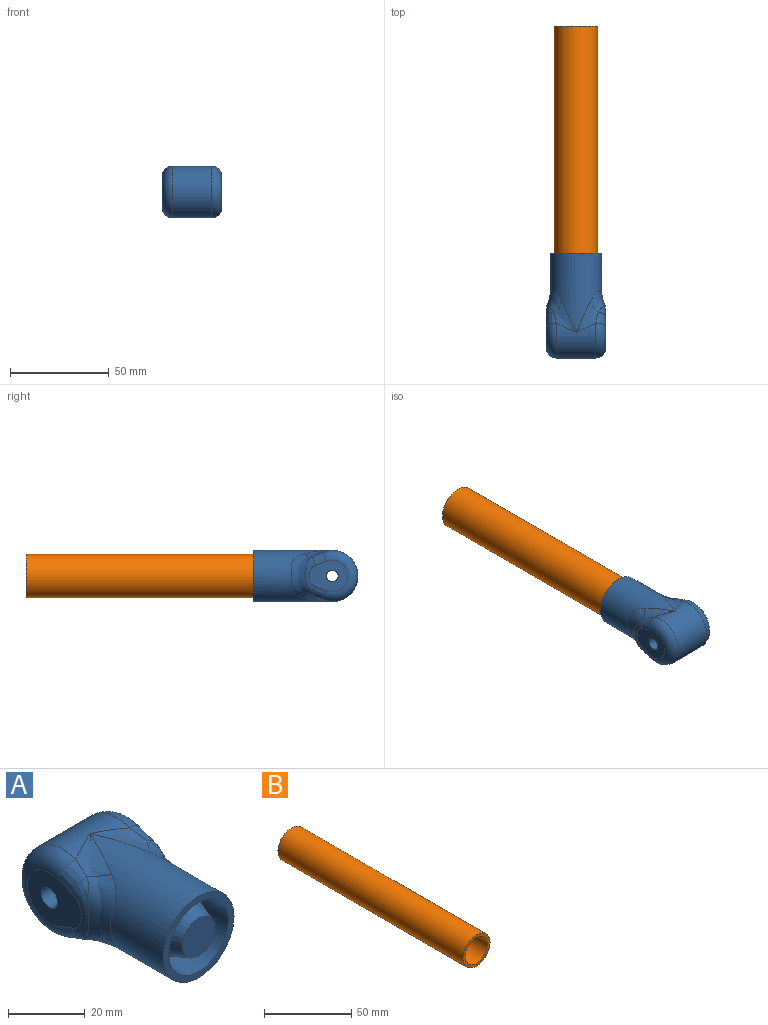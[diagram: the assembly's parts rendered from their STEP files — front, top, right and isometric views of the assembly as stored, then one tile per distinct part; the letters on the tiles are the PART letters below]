
ASSEMBLY  parts=2 mates=1
PART A: 26 faces, bbox 32.6x54.1x30.8 mm
  f0: cylinder r=11mm len=35mm, axis (0,1,0), area 2419mm2, adj f1,f5
  f1: plane 22x22mm, normal (0,-1,0), area 125.7mm2, adj f0,f2
  f2: cylinder r=9mm len=26.76mm, axis (0,1,0), area 1513.1mm2, adj f1,f3
  f3: cone r=6mm half-angle=20deg, axis (0,1,0), area 413.3mm2, adj f2,f4
  f4: plane 12x12mm, normal (0,-1,0), area 113.1mm2, adj f3
  f5: plane 26x26mm, normal (0,-1,0), area 150.8mm2, adj f0,f6
  f6: cylinder r=13mm len=40mm, axis (0,1,0), area 2262.5mm2, adj f5,f7,f20,f21,f22,f23,f24,f25
  f7: bspline ~16.32x16.32mm, area 62.4mm2, adj f6,f8,f19,f20
  f8: bspline ~12.76x9.34mm, area 42.6mm2, adj f7,f9,f17,f18
  f9: plane 19.77x16mm, normal (1,0,0), area 216.3mm2, adj f8,f10,f16,f17,f18
  f10: cylinder r=3mm len=30mm, axis (-1,0,0), area 565.5mm2, adj f9,f11
  f11: plane 19.77x16mm, normal (-1,0,0), area 216.3mm2, adj f10,f12,f13,f14,f15
  f12: bspline ~15.49x11.01mm, area 42.6mm2, adj f11,f13,f15,f24
  f13: bspline ~20.29x5.91mm, area 66.1mm2, adj f11,f12,f14,f23
  f14: bspline ~15.07x10.85mm, area 42.6mm2, adj f11,f13,f15,f22
  f15: torus R=8mm, axis (1,0,0), area 340.1mm2, adj f11,f12,f14,f19
  f16: bspline ~9.9x7.76mm, area 42.6mm2, adj f9,f17,f18,f21
  f17: bspline ~20.81x6.73mm, area 66.1mm2, adj f8,f9,f16,f20
  f18: torus R=8mm, axis (1,0,0), area 340.1mm2, adj f8,f9,f16,f19
  f19: cylinder r=13mm len=26mm, axis (-1,0,0), area 911.8mm2, adj f7,f15,f18,f21,f22,f24,f25
  f20: bspline ~22.75x14.97mm, area 152.8mm2, adj f6,f7,f17,f21
  f21: bspline ~16.32x16.32mm, area 47.2mm2, adj f6,f16,f19,f20
  f22: bspline ~16.32x16.32mm, area 47.2mm2, adj f6,f14,f19,f23
  f23: bspline ~22.75x14.97mm, area 152.8mm2, adj f6,f13,f22,f24
  f24: bspline ~16.32x16.32mm, area 54.8mm2, adj f6,f12,f19,f23
  f25: bspline ~3.66x3.66mm, area 0mm2, adj f6,f19
PART B: 4 faces, bbox 22x150x22 mm
  f0: cylinder r=9mm len=150mm, axis (0,1,0), area 8482.3mm2, adj f2,f3
  f1: cylinder r=11mm len=150mm, axis (0,1,0), area 10367.3mm2, adj f2,f3
  f2: plane 22x22mm, normal (0,-1,0), area 125.7mm2, adj f0,f1
  f3: plane 22x22mm, normal (0,1,0), area 125.7mm2, adj f0,f1
PLACE A rot(axis=(-1,0,0),180deg) t=(-50.14,-127.85,4.75)mm
PLACE B t=(-50.14,27.15,4.75)mm
MATE cylindrical A.f0 <-> B.f0  axis (0,1,0) through (-50.14,-122.85,4.75)mm
